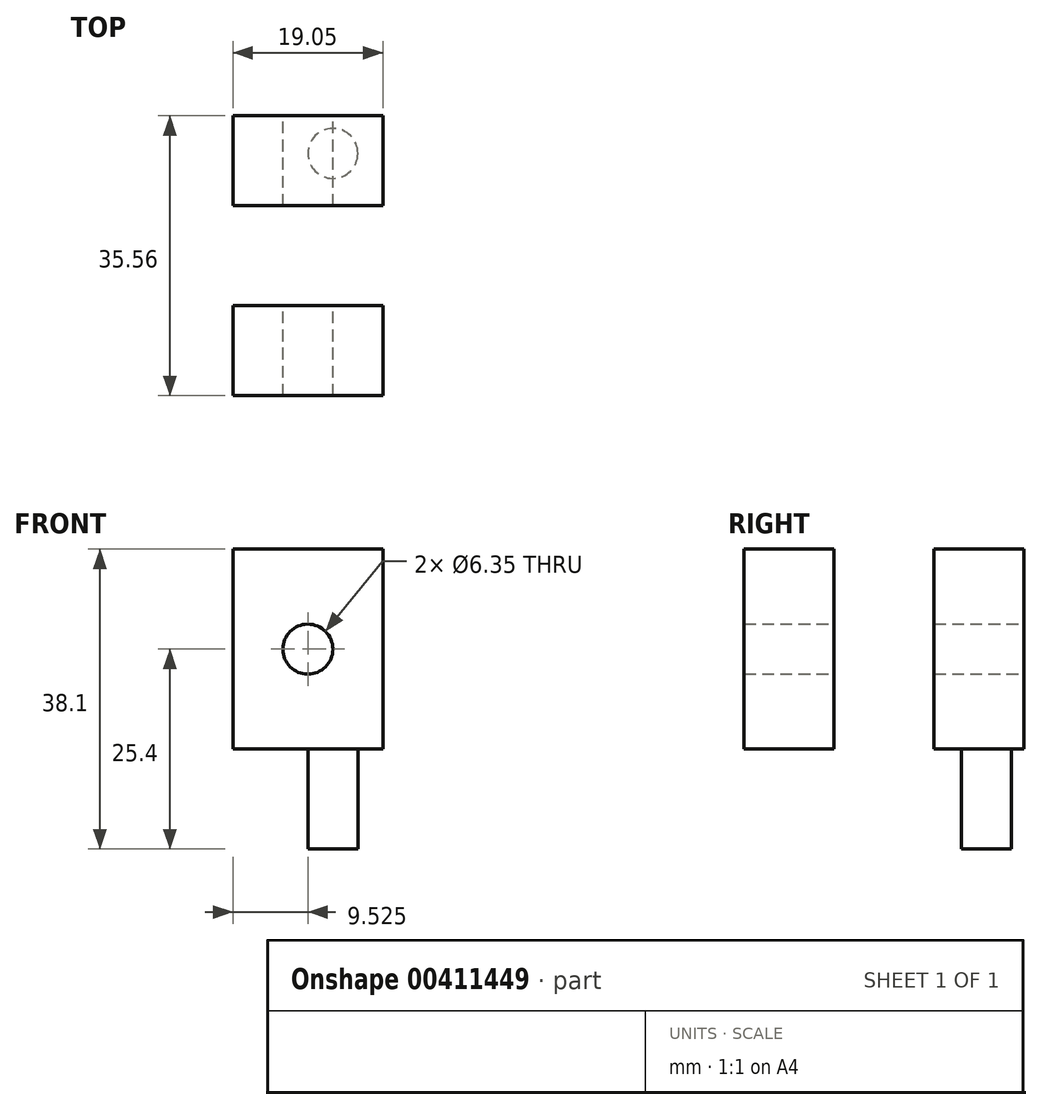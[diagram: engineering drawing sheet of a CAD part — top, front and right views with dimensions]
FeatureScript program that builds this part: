
annotation { "Feature Type Name" : "Feature", "Feature Type Description" : "" }
export const myFeature = defineFeature(function(context is Context, id is Id, definition is map)
    precondition{}
    {
        {
            var Q0;
            Q0=qCreatedBy(makeId("Right.planeOp"),FACE);
            var sketch = newSketch(context, id + "F0", { "sketchPlane" : qUnion([Q0])});
            skLineSegment(sketch, "E0.bottom", {"start": v(-17.78, 31.75) * mm, "end": v(-6.35, 31.75) * mm});
            skLineSegment(sketch, "E0.top", {"start": v(-17.78, -6.35) * mm, "end": v(-6.35, -6.35) * mm});
            skLineSegment(sketch, "E0.left", {"start": v(-17.78, 31.75) * mm, "end": v(-17.78, -6.35) * mm});
            skLineSegment(sketch, "E0.right", {"start": v(-6.35, 31.75) * mm, "end": v(-6.35, 0) * mm});
            skLineSegment(sketch, "E1.bottom", {"start": v(-6.35, 0) * mm, "end": v(6.35, 0) * mm});
            skLineSegment(sketch, "E1.top", {"start": v(-17.78, -6.35) * mm, "end": v(17.78, -6.35) * mm});
            skLineSegment(sketch, "E1.left", {"start": v(-17.78, 0) * mm, "end": v(-17.78, -6.35) * mm});
            skLineSegment(sketch, "E1.right", {"start": v(17.78, 0) * mm, "end": v(17.78, -6.35) * mm});
            skLineSegment(sketch, "E2.bottom", {"start": v(17.78, -6.35) * mm, "end": v(6.35, -6.35) * mm});
            skLineSegment(sketch, "E2.top", {"start": v(17.78, 31.75) * mm, "end": v(6.35, 31.75) * mm});
            skLineSegment(sketch, "E2.left", {"start": v(17.78, -6.35) * mm, "end": v(17.78, 31.75) * mm});
            skLineSegment(sketch, "E2.right", {"start": v(6.35, 0) * mm, "end": v(6.35, 31.75) * mm});
            skSolve(sketch);
        }
        {
            var Q0;
            Q0=makeQuery(id+"F0.imprint","IMPRINT",FACE,{"disambiguationData":[TD([[makeQuery(id+"F0.imprint","IMPRINT",EDGE,{"derivedFrom":sQuery(id+"F0.wireOp",EDGE,"E0.bottom")}),-1.0]])]});
            extrude(context, id + "F1", {"entities" : qUnion([Q0]), "depth" : 19.05 * mm});
        }
        {
            var Q0;
            Q0=makeQuery(id+"F1.opExtrude","SWEPT_FACE",FACE,{"disambiguationData":[OSD([sQuery(id+"F0.wireOp",EDGE,"E2.left")])]});
            var sketch = newSketch(context, id + "F2", { "sketchPlane" : qUnion([Q0])});
            skCircle(sketch, "E3", {"center": v(-9.53, 19.05) * mm, "radius": 3.18 * mm});
            skSolve(sketch);
        }
        {
            var Q0;
            Q0=makeQuery(id+"F2.imprint","IMPRINT",FACE,{"disambiguationData":[TD([[makeQuery(id+"F2.imprint","IMPRINT",EDGE,{"derivedFrom":sQuery(id+"F2.wireOp",EDGE,"E3")}),1.0]])]});
            extrude(context, id + "F3", {"entities" : qUnion([Q0]), "operationType" : NewBodyOperationType.REMOVE, "endBound" : BoundingType.THROUGH_ALL, "oppositeDirection" : true, "depth" : 25.4 * mm});
        }
        {
            var Q0;
            Q0=makeQuery(id+"F1.opExtrude","SWEPT_FACE",FACE,{"disambiguationData":[OSD([sQuery(id+"F0.wireOp",EDGE,"E1.top"),sQuery(id+"F0.wireOp",EDGE,"E2.bottom")])]});
            var sketch = newSketch(context, id + "F4", { "sketchPlane" : qUnion([Q0])});
            skCircle(sketch, "E4", {"center": v(12.7, 13) * mm, "radius": 3.18 * mm});
            skCircle(sketch, "E5.MirrorC", {"center": v(12.7, -13) * mm, "radius": 3.18 * mm});
            skSolve(sketch);
        }
        {
            var Q0;
            Q0=makeQuery(id+"F4.imprint","IMPRINT",FACE,{"disambiguationData":[TD([[makeQuery(id+"F4.imprint","IMPRINT",EDGE,{"derivedFrom":sQuery(id+"F4.wireOp",EDGE,"E4")}),1.0]])]});
            var Q1;
            Q1=makeQuery(id+"F4.imprint","IMPRINT",FACE,{"disambiguationData":[TD([[makeQuery(id+"F4.imprint","IMPRINT",EDGE,{"derivedFrom":sQuery(id+"F4.wireOp",EDGE,"E5.MirrorC")}),-1.0]])]});
            extrude(context, id + "F5", {"entities" : qUnion([Q0, Q1]), "operationType" : NewBodyOperationType.REMOVE, "oppositeDirection" : true, "depth" : 12.7 * mm});
        }
    });
